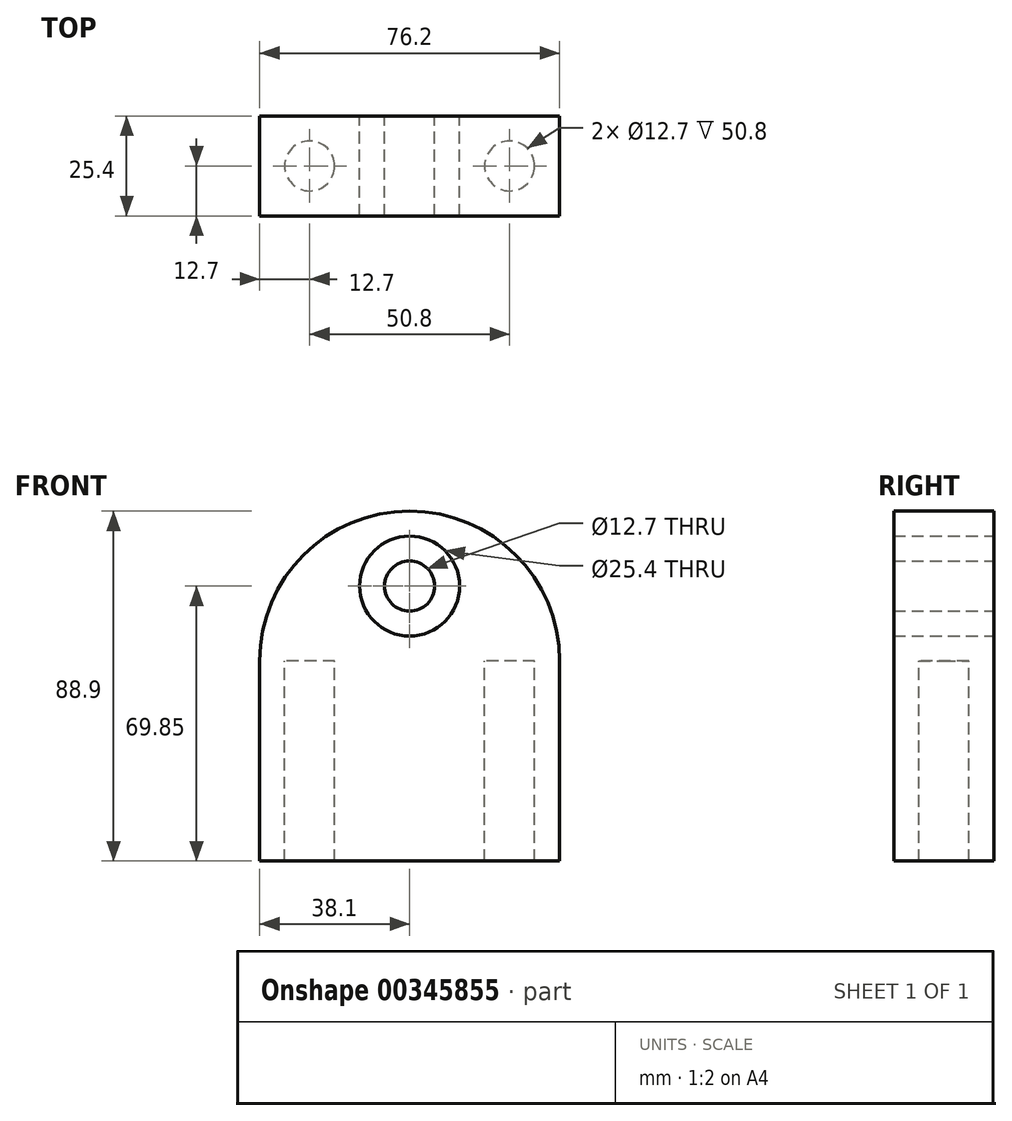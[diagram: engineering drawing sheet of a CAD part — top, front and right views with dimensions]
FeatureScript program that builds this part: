
annotation { "Feature Type Name" : "Feature", "Feature Type Description" : "" }
export const myFeature = defineFeature(function(context is Context, id is Id, definition is map)
    precondition{}
    {
        {
            var Q0;
            Q0=qCreatedBy(makeId("Front.planeOp"),FACE);
            var sketch = newSketch(context, id + "F4", { "sketchPlane" : qUnion([Q0])});
            skArc(sketch, "E0", {"start": v(38.1, 0) * mm, "mid": v(0, 38.1) * mm, "end": v(-38.1, 0) * mm});
            skLineSegment(sketch, "E1", {"start": v(-38.1, 0) * mm, "end": v(38.1, 0) * mm});
            skCircle(sketch, "E2", {"center": v(0, 19.05) * mm, "radius": 12.7 * mm});
            skCircle(sketch, "E3", {"center": v(0, 19.05) * mm, "radius": 6.35 * mm});
            skLineSegment(sketch, "E4.left", {"start": v(-38.1, 0) * mm, "end": v(-38.1, -50.8) * mm});
            skLineSegment(sketch, "E4.right", {"start": v(38.1, 0) * mm, "end": v(38.1, -50.8) * mm});
            skLineSegment(sketch, "E5", {"start": v(-38.1, -50.8) * mm, "end": v(38.1, -50.8) * mm});
            skPoint(sketch, "E4.top.end.orphan", {"position": v(38.1, -101.6) * mm});
            skPoint(sketch, "E6.orphan", {"position": v(-38.1, -101.6) * mm});
            skSolve(sketch);
        }
        {
            var Q0;
            Q0=makeQuery(id+"F4.imprint","IMPRINT",FACE,{"disambiguationData":[TD([[makeQuery(id+"F4.imprint","IMPRINT",EDGE,{"derivedFrom":sQuery(id+"F4.wireOp",EDGE,"E0")}),1.0]])]});
            var Q1;
            Q1=makeQuery(id+"F4.imprint","IMPRINT",FACE,{"disambiguationData":[TD([[makeQuery(id+"F4.imprint","IMPRINT",EDGE,{"derivedFrom":sQuery(id+"F4.wireOp",EDGE,"E1")}),-1.0]])]});
            extrude(context, id + "F0", {"entities" : qUnion([Q0, Q1]), "depth" : 25.4 * mm});
        }
        {
            var Q0;
            Q0=makeQuery(id+"F4.imprint","IMPRINT",FACE,{"disambiguationData":[TD([[makeQuery(id+"F4.imprint","IMPRINT",EDGE,{"derivedFrom":sQuery(id+"F4.wireOp",EDGE,"E2")}),1.0]])]});
            var Q1;
            Q1=sQuery(id+"F4.wireOp",EDGE,"E2");
            extrude(context, id + "F1", {"entities" : qUnion([Q0]), "surfaceEntities" : qUnion([Q1]), "depth" : 25.4 * mm});
        }
        {
            var Q0;
            Q0=qCreatedBy(makeId("Top.planeOp"),FACE);
            var sketch = newSketch(context, id + "F2", { "sketchPlane" : qUnion([Q0])});
            skPoint(sketch, "E7", {"position": v(25.4, 0) * mm});
            skPoint(sketch, "E8", {"position": v(-25.4, 0) * mm});
            skPoint(sketch, "E9", {"position": v(25.4, -12.7) * mm});
            skPoint(sketch, "E10", {"position": v(-25.4, -12.7) * mm});
            skSolve(sketch);
        }
        {
            var Q0;
            Q0=sQuery(id+"F2.wireOp",VERTEX,"E10");
            var Q1;
            Q1=sQuery(id+"F2.wireOp",VERTEX,"E9");
            var Q2;
            Q2=makeQuery(id+"F0.opExtrude","SWEPT_BODY",BODY,{"disambiguationData":[OSD([sQuery(id+"F4.wireOp",EDGE,"E0"),sQuery(id+"F4.wireOp",EDGE,"E2"),sQuery(id+"F4.wireOp",EDGE,"E4.left"),sQuery(id+"F4.wireOp",EDGE,"E4.right"),sQuery(id+"F4.wireOp",EDGE,"E5")])]});
            hole(context, id + "F3", {"style" : HoleStyle.SIMPLE, "endStyle" : HoleEndStyle.THROUGH, "holeDiameter" : 12.7 * mm, "locations" : qUnion([Q0, Q1]), "scope" : qUnion([Q2]), "isTappedThrough" : true});
        }
    });
